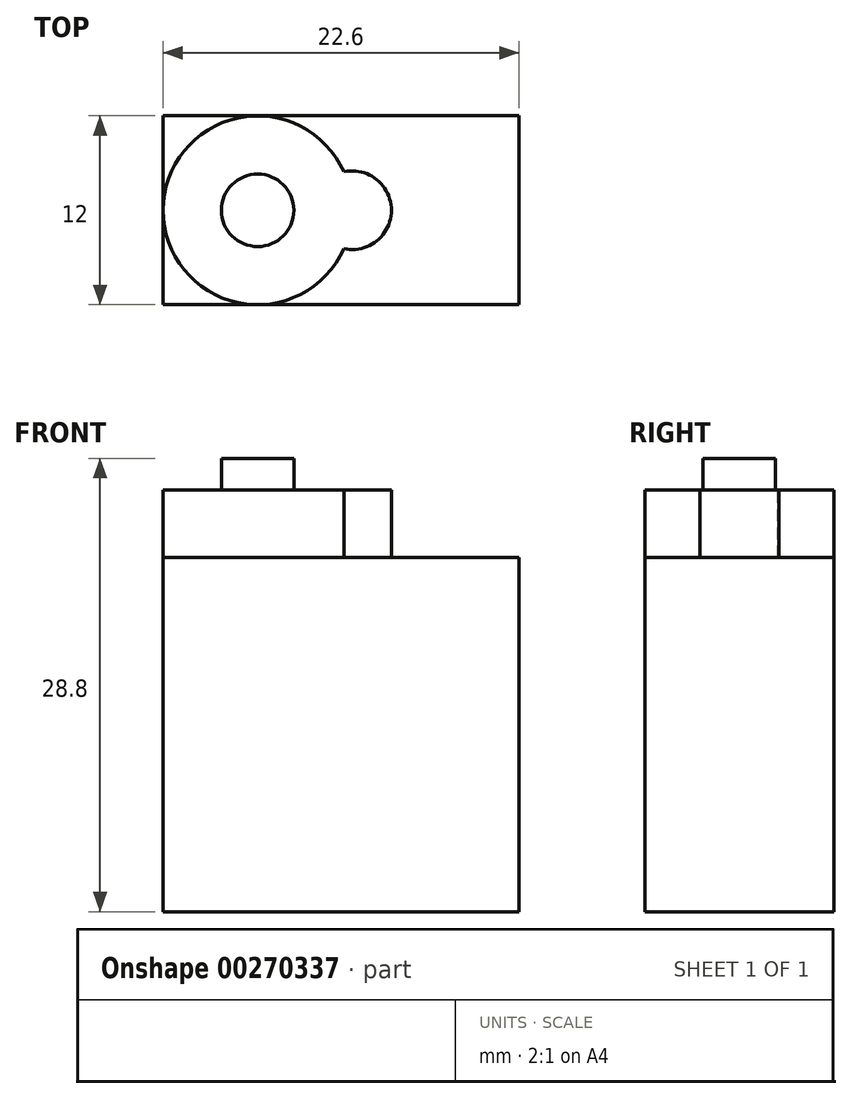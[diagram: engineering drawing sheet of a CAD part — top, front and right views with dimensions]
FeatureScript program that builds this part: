
annotation { "Feature Type Name" : "Feature", "Feature Type Description" : "" }
export const myFeature = defineFeature(function(context is Context, id is Id, definition is map)
    precondition{}
    {
        {
            var Q0;
            Q0=qCreatedBy(makeId("Top.planeOp"),FACE);
            var sketch = newSketch(context, id + "F0", { "sketchPlane" : qUnion([Q0])});
            skLineSegment(sketch, "E0.bottom", {"start": v(11.3, -6) * mm, "end": v(-11.3, -6) * mm});
            skLineSegment(sketch, "E0.top", {"start": v(11.3, 6) * mm, "end": v(-11.3, 6) * mm});
            skLineSegment(sketch, "E0.left", {"start": v(11.3, -6) * mm, "end": v(11.3, 6) * mm});
            skLineSegment(sketch, "E0.right", {"start": v(-11.3, -6) * mm, "end": v(-11.3, 6) * mm});
            skPoint(sketch, "E0.middle", {"position": v(0, 0) * mm});
            skSolve(sketch);
        }
        {
            var Q0;
            Q0 = qSketchRegion(id + "F0", true);
            extrude(context, id + "F1", {"entities" : qUnion([Q0]), "depth" : 22.5 * mm});
        }
        {
            var Q0;
            Q0=makeQuery(id+"F1.opExtrude","CAP_FACE",FACE,{"disambiguationData":[OSD([sQuery(id+"F0.wireOp",EDGE,"E0.bottom"),sQuery(id+"F0.wireOp",EDGE,"E0.top"),sQuery(id+"F0.wireOp",EDGE,"E0.left"),sQuery(id+"F0.wireOp",EDGE,"E0.right")])],"isStart":false});
            var sketch = newSketch(context, id + "F2", { "sketchPlane" : qUnion([Q0])});
            skCircle(sketch, "E1", {"center": v(-5.3, 0) * mm, "radius": 6 * mm});
            skPoint(sketch, "E1.centerSnap0", {"position": v(-11.3, 0) * mm});
            skSolve(sketch);
        }
        {
            var Q0;
            Q0 = qSketchRegion(id + "F2", true);
            extrude(context, id + "F3", {"entities" : qUnion([Q0]), "operationType" : NewBodyOperationType.ADD, "depth" : 4.3 * mm});
        }
        {
            var Q0;
            Q0=makeQuery(id+"F3.opExtrude","CAP_FACE",FACE,{"disambiguationData":[OSD([sQuery(id+"F2.wireOp",EDGE,"E1")])],"isStart":false});
            var sketch = newSketch(context, id + "F4", { "sketchPlane" : qUnion([Q0])});
            skCircle(sketch, "E2", {"center": v(-5.3, 0) * mm, "radius": 2.3 * mm});
            skSolve(sketch);
        }
        {
            var Q0;
            Q0 = qSketchRegion(id + "F4", true);
            extrude(context, id + "F5", {"entities" : qUnion([Q0]), "operationType" : NewBodyOperationType.ADD, "depth" : 2 * mm});
        }
        {
            var Q0;
            Q0=makeQuery(id+"F3.opExtrude","CAP_FACE",FACE,{"disambiguationData":[OSD([sQuery(id+"F2.wireOp",EDGE,"E1")])],"isStart":false});
            var sketch = newSketch(context, id + "F6", { "sketchPlane" : qUnion([Q0])});
            skCircle(sketch, "E3", {"center": v(0.7, 0) * mm, "radius": 2.5 * mm});
            skSolve(sketch);
        }
        {
            var Q0;
            Q0 = qSketchRegion(id + "F6", true);
            extrude(context, id + "F7", {"entities" : qUnion([Q0]), "operationType" : NewBodyOperationType.ADD, "oppositeDirection" : true, "depth" : 5 * mm});
        }
    });
